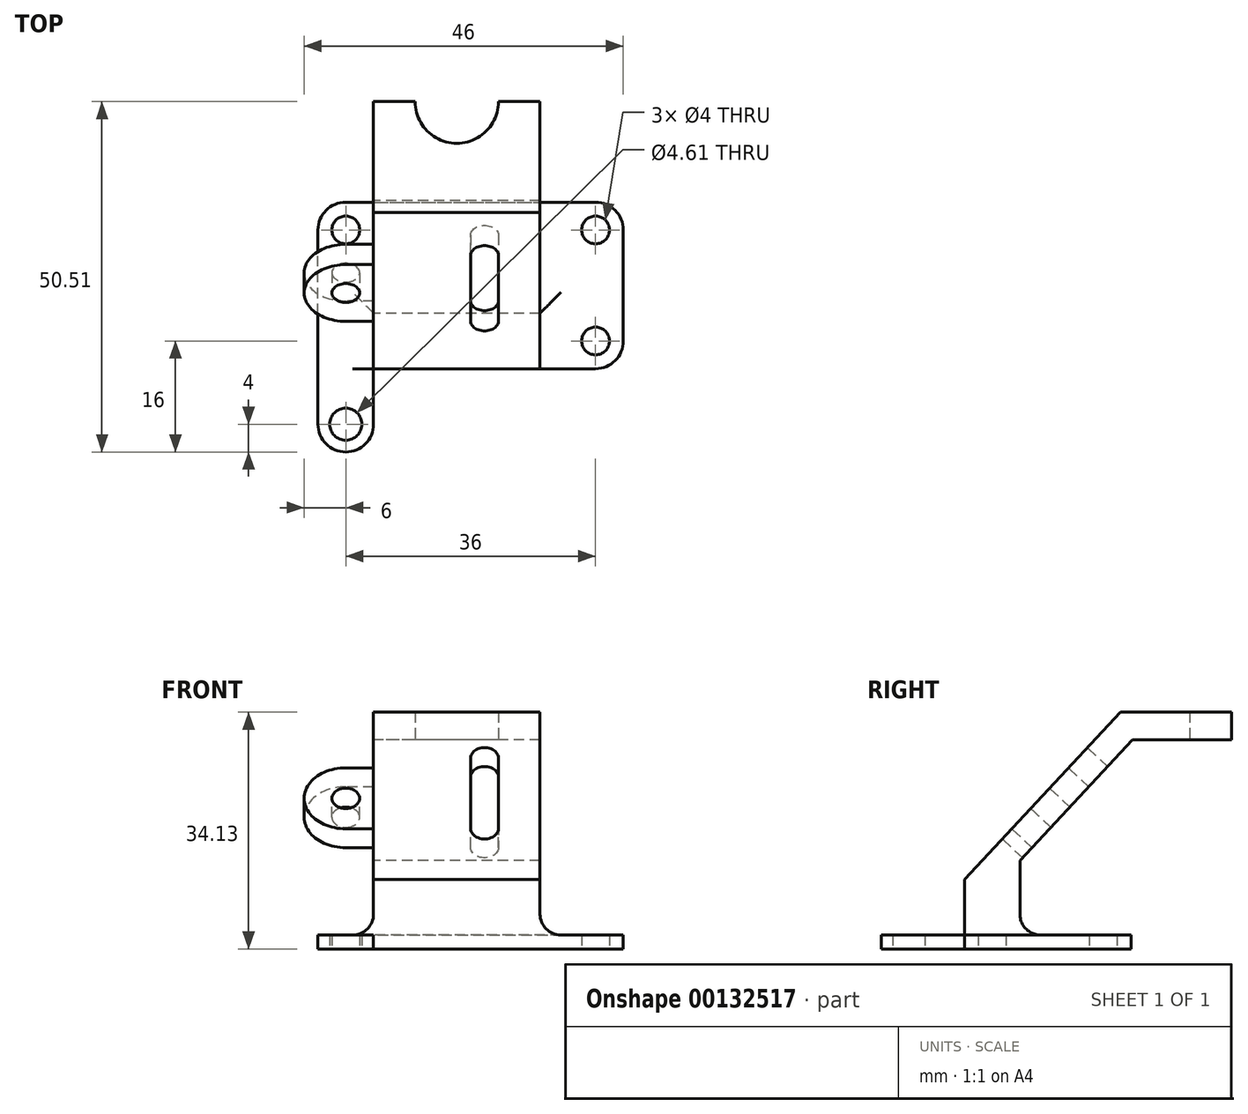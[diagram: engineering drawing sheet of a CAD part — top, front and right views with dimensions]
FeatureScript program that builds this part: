
annotation { "Feature Type Name" : "Feature", "Feature Type Description" : "" }
export const myFeature = defineFeature(function(context is Context, id is Id, definition is map)
    precondition{}
    {
        {
            var Q0;
            Q0=qCreatedBy(makeId("Top.planeOp"),FACE);
            var sketch = newSketch(context, id + "F0", { "sketchPlane" : qUnion([Q0])});
            skLineSegment(sketch, "E0", {"start": v(0, 0) * mm, "end": v(0, 24) * mm});
            skLineSegment(sketch, "E1", {"start": v(0, 24) * mm, "end": v(44, 24) * mm});
            skLineSegment(sketch, "E2", {"start": v(44, 24) * mm, "end": v(44, 0) * mm});
            skLineSegment(sketch, "E3", {"start": v(44, 0) * mm, "end": v(8, 0) * mm});
            skLineSegment(sketch, "E4", {"start": v(8, 0) * mm, "end": v(8, -8) * mm});
            skLineSegment(sketch, "E5", {"start": v(0, 0) * mm, "end": v(0, -8) * mm});
            skArc(sketch, "E6", {"start": v(0, -8) * mm, "mid": v(4, -12) * mm, "end": v(8, -8) * mm});
            skCircle(sketch, "E7", {"center": v(4, -8) * mm, "radius": 2.3 * mm});
            skCircle(sketch, "E8", {"center": v(40, 4) * mm, "radius": 2 * mm});
            skCircle(sketch, "E9", {"center": v(40, 20) * mm, "radius": 2 * mm});
            skCircle(sketch, "E10", {"center": v(4, 20) * mm, "radius": 2 * mm});
            skSolve(sketch);
        }
        {
            var Q0;
            Q0=makeQuery(id+"F0.imprint","IMPRINT",FACE,{"disambiguationData":[TD([[makeQuery(id+"F0.imprint","IMPRINT",EDGE,{"derivedFrom":sQuery(id+"F0.wireOp",EDGE,"E0")}),-1.0]])]});
            extrude(context, id + "F1", {"entities" : qUnion([Q0]), "depth" : 2 * mm});
        }
        {
            var Q0;
            Q0=makeQuery(id+"F1.opExtrude","SWEPT_FACE",FACE,{"disambiguationData":[OSD([sQuery(id+"F0.wireOp",EDGE,"E4")])]});
            var sketch = newSketch(context, id + "F2", { "sketchPlane" : qUnion([Q0])});
            skLineSegment(sketch, "E11", {"start": v(0, 0) * mm, "end": v(0, 10) * mm});
            skLineSegment(sketch, "E12", {"start": v(0, 10) * mm, "end": v(22.5, 34.13) * mm});
            skLineSegment(sketch, "E13", {"start": v(22.5, 34.13) * mm, "end": v(38.5, 34.13) * mm});
            skLineSegment(sketch, "E14", {"start": v(38.5, 34.13) * mm, "end": v(38.5, 30.13) * mm});
            skLineSegment(sketch, "E15", {"start": v(38.5, 30.13) * mm, "end": v(24.25, 30.13) * mm});
            skLineSegment(sketch, "E16", {"start": v(24.25, 30.13) * mm, "end": v(8, 12.71) * mm});
            skLineSegment(sketch, "E17", {"start": v(8, 12.71) * mm, "end": v(8, 0) * mm});
            skLineSegment(sketch, "E18", {"start": v(8, 0) * mm, "end": v(0, 0) * mm});
            skLineSegment(sketch, "E19", {"start": v(8, 12.71) * mm, "end": v(28.06, 12.71) * mm, "construction": true});
            skSolve(sketch);
        }
        {
            var Q0;
            {var subQ0=sQuery(id+"F2.wireOp",EDGE,"E12");Q0=makeQuery(id+"F2.imprint","IMPRINT",FACE,{"disambiguationData":[TD([[makeQuery(id+"F2.imprint","IMPRINT",EDGE,{"derivedFrom":subQ0}),-1.0]])]});}
            extrude(context, id + "F3", {"entities" : qUnion([Q0]), "operationType" : NewBodyOperationType.ADD, "depth" : 24 * mm});
        }
        {
            var Q0;
            Q0=makeQuery(id+"F3.opExtrude","SWEPT_FACE",FACE,{"disambiguationData":[OSD([sQuery(id+"F2.wireOp",EDGE,"E12")])]});
            var sketch = newSketch(context, id + "F4", { "sketchPlane" : qUnion([Q0])});
            skLineSegment(sketch, "E20", {"start": v(8, 7.31) * mm, "end": v(32, 7.31) * mm});
            skLineSegment(sketch, "E21", {"start": v(32, 7.31) * mm, "end": v(32, 40.31) * mm});
            skLineSegment(sketch, "E22", {"start": v(32, 40.31) * mm, "end": v(8, 40.31) * mm});
            skLineSegment(sketch, "E23", {"start": v(8, 40.31) * mm, "end": v(8, 29.31) * mm});
            skLineSegment(sketch, "E24", {"start": v(8, 29.31) * mm, "end": v(4, 29.31) * mm});
            skLineSegment(sketch, "E25", {"start": v(8, 7.31) * mm, "end": v(8, 17.31) * mm});
            skLineSegment(sketch, "E26", {"start": v(8, 17.31) * mm, "end": v(4, 17.31) * mm});
            skArc(sketch, "E27", {"start": v(4, 29.31) * mm, "mid": v(-2, 23.31) * mm, "end": v(4, 17.31) * mm});
            skCircle(sketch, "E28", {"center": v(4, 23.31) * mm, "radius": 2 * mm});
            skLineSegment(sketch, "E29", {"start": v(22, 17.31) * mm, "end": v(22, 31.31) * mm});
            skLineSegment(sketch, "E30", {"start": v(26, 31.31) * mm, "end": v(26, 17.31) * mm});
            skArc(sketch, "E31", {"start": v(26, 31.31) * mm, "mid": v(24, 33.31) * mm, "end": v(22, 31.31) * mm});
            skArc(sketch, "E32", {"start": v(22, 17.31) * mm, "mid": v(24, 15.31) * mm, "end": v(26, 17.31) * mm});
            skSolve(sketch);
        }
        {
            var Q0;
            {var subQ1=sQuery(id+"F4.wireOp",EDGE,"E24");Q0=makeQuery(id+"F4.imprint","IMPRINT",FACE,{"disambiguationData":[TD([[makeQuery(id+"F4.imprint","IMPRINT",EDGE,{"derivedFrom":subQ1}),1.0]])]});}
            extrude(context, id + "F5", {"entities" : qUnion([Q0]), "oppositeDirection" : true, "depth" : 4 * mm});
        }
        {
            var Q0;
            Q0=makeQuery(id+"F4.imprint","IMPRINT",FACE,{"disambiguationData":[TD([[makeQuery(id+"F4.imprint","IMPRINT",EDGE,{"derivedFrom":sQuery(id+"F4.wireOp",EDGE,"E29")}),-1.0]])]});
            extrude(context, id + "F6", {"entities" : qUnion([Q0]), "operationType" : NewBodyOperationType.REMOVE, "endBound" : BoundingType.UP_TO_NEXT, "oppositeDirection" : true, "depth" : 25 * mm});
        }
        {
            var Q0;
            Q0=makeQuery(id+"F3.boolean.opBoolean","INTERSECT",EDGE,{"derivedFrom":[makeQuery(id+"F1.opExtrude","CAP_FACE",FACE,{"disambiguationData":[OSD([sQuery(id+"F0.wireOp",EDGE,"E0"),sQuery(id+"F0.wireOp",EDGE,"E1"),sQuery(id+"F0.wireOp",EDGE,"E2"),sQuery(id+"F0.wireOp",EDGE,"E3"),sQuery(id+"F0.wireOp",EDGE,"E4"),sQuery(id+"F0.wireOp",EDGE,"E5"),sQuery(id+"F0.wireOp",EDGE,"E6"),sQuery(id+"F0.wireOp",EDGE,"E7"),sQuery(id+"F0.wireOp",EDGE,"E8"),sQuery(id+"F0.wireOp",EDGE,"E9"),sQuery(id+"F0.wireOp",EDGE,"E10")])],"isStart":false}),makeQuery(id+"F3.opExtrude","CAP_FACE",FACE,{"disambiguationData":[OSD([sQuery(id+"F2.wireOp",EDGE,"E11"),sQuery(id+"F2.wireOp",EDGE,"E12"),sQuery(id+"F2.wireOp",EDGE,"E13"),sQuery(id+"F2.wireOp",EDGE,"E14"),sQuery(id+"F2.wireOp",EDGE,"E15"),sQuery(id+"F2.wireOp",EDGE,"E16"),sQuery(id+"F2.wireOp",EDGE,"E17"),sQuery(id+"F2.wireOp",EDGE,"E18")])],"isStart":false})]});
            fillet(context, id + "F7", {"entities" : qUnion([Q0]), "radius" : 3 * mm, "tangentPropagation" : true, "allowEdgeOverflow" : false});
        }
        {
            var Q0;
            Q0=makeQuery(id+"F1.opExtrude","SWEPT_EDGE",EDGE,{"disambiguationData":[OSD([sQuery(id+"F0.wireOp",EDGE,"E2"),sQuery(id+"F0.wireOp",EDGE,"E3")])]});
            fillet(context, id + "F8", {"entities" : qUnion([Q0]), "radius" : 4 * mm, "tangentPropagation" : true, "allowEdgeOverflow" : false});
        }
        {
            var Q0;
            Q0=makeQuery(id+"F1.opExtrude","SWEPT_EDGE",EDGE,{"disambiguationData":[OSD([sQuery(id+"F0.wireOp",EDGE,"E1"),sQuery(id+"F0.wireOp",EDGE,"E2")])]});
            fillet(context, id + "F9", {"entities" : qUnion([Q0]), "radius" : 4 * mm, "tangentPropagation" : true, "allowEdgeOverflow" : false});
        }
        {
            var Q0;
            Q0=makeQuery(id+"F1.opExtrude","SWEPT_EDGE",EDGE,{"disambiguationData":[OSD([sQuery(id+"F0.wireOp",EDGE,"E0"),sQuery(id+"F0.wireOp",EDGE,"E1")])]});
            fillet(context, id + "F10", {"entities" : qUnion([Q0]), "radius" : 4 * mm, "tangentPropagation" : true, "allowEdgeOverflow" : false});
        }
        {
            var Q0;
            Q0=makeQuery(id+"F3.boolean.opBoolean","INTERSECT",EDGE,{"derivedFrom":[makeQuery(id+"F1.opExtrude","CAP_FACE",FACE,{"disambiguationData":[OSD([sQuery(id+"F0.wireOp",EDGE,"E0"),sQuery(id+"F0.wireOp",EDGE,"E1"),sQuery(id+"F0.wireOp",EDGE,"E2"),sQuery(id+"F0.wireOp",EDGE,"E3"),sQuery(id+"F0.wireOp",EDGE,"E4"),sQuery(id+"F0.wireOp",EDGE,"E5"),sQuery(id+"F0.wireOp",EDGE,"E6"),sQuery(id+"F0.wireOp",EDGE,"E7"),sQuery(id+"F0.wireOp",EDGE,"E8"),sQuery(id+"F0.wireOp",EDGE,"E9"),sQuery(id+"F0.wireOp",EDGE,"E10")])],"isStart":false}),makeQuery(id+"F3.opExtrude","SWEPT_FACE",FACE,{"disambiguationData":[OSD([sQuery(id+"F2.wireOp",EDGE,"E17")])]})]});
            fillet(context, id + "F11", {"entities" : qUnion([Q0]), "radius" : 3 * mm, "tangentPropagation" : true, "allowEdgeOverflow" : false});
        }
        {
            var Q0;
            Q0=makeQuery(id+"F3.boolean.opBoolean","INTERSECT",EDGE,{"derivedFrom":[makeQuery(id+"F1.opExtrude","CAP_FACE",FACE,{"disambiguationData":[OSD([sQuery(id+"F0.wireOp",EDGE,"E0"),sQuery(id+"F0.wireOp",EDGE,"E1"),sQuery(id+"F0.wireOp",EDGE,"E2"),sQuery(id+"F0.wireOp",EDGE,"E3"),sQuery(id+"F0.wireOp",EDGE,"E4"),sQuery(id+"F0.wireOp",EDGE,"E5"),sQuery(id+"F0.wireOp",EDGE,"E6"),sQuery(id+"F0.wireOp",EDGE,"E7"),sQuery(id+"F0.wireOp",EDGE,"E8"),sQuery(id+"F0.wireOp",EDGE,"E9"),sQuery(id+"F0.wireOp",EDGE,"E10")])],"isStart":false}),makeQuery(id+"F3.opExtrude","CAP_FACE",FACE,{"disambiguationData":[OSD([sQuery(id+"F2.wireOp",EDGE,"E11"),sQuery(id+"F2.wireOp",EDGE,"E12"),sQuery(id+"F2.wireOp",EDGE,"E13"),sQuery(id+"F2.wireOp",EDGE,"E14"),sQuery(id+"F2.wireOp",EDGE,"E15"),sQuery(id+"F2.wireOp",EDGE,"E16"),sQuery(id+"F2.wireOp",EDGE,"E17"),sQuery(id+"F2.wireOp",EDGE,"E18")])],"isStart":true})]});
            fillet(context, id + "F12", {"entities" : qUnion([Q0]), "radius" : 3 * mm, "tangentPropagation" : true, "allowEdgeOverflow" : false});
        }
        {
            var Q0;
            Q0=qCreatedBy(makeId("Top.planeOp"),FACE);
            var sketch = newSketch(context, id + "F13", { "sketchPlane" : qUnion([Q0])});
            skLineSegment(sketch, "E33", {"start": v(0, 0) * mm, "end": v(44, 0) * mm});
            skLineSegment(sketch, "E34", {"start": v(44, 0) * mm, "end": v(44, 38.5) * mm});
            skLineSegment(sketch, "E35", {"start": v(44, 38.5) * mm, "end": v(0, 38.5) * mm});
            skLineSegment(sketch, "E36", {"start": v(0, 38.5) * mm, "end": v(0, 0) * mm});
            skArc(sketch, "E37", {"start": v(14, 38.5) * mm, "mid": v(20, 32.5) * mm, "end": v(26, 38.5) * mm});
            skLineSegment(sketch, "E38", {"start": v(14, 38.5) * mm, "end": v(26, 38.5) * mm});
            skSolve(sketch);
        }
        {
            var Q0;
            Q0=makeQuery(id+"F13.imprint","IMPRINT",FACE,{"disambiguationData":[TD([[makeQuery(id+"F13.imprint","IMPRINT",EDGE,{"derivedFrom":sQuery(id+"F13.wireOp",EDGE,"E37")}),1.0]])]});
            var Q1;
            Q1=sQuery(id+"F13.wireOp",EDGE,"E37");
            var Q2;
            Q2=sQuery(id+"F13.wireOp",EDGE,"E38");
            extrude(context, id + "F14", {"entities" : qUnion([Q0]), "operationType" : NewBodyOperationType.REMOVE, "surfaceEntities" : qUnion([Q1, Q2]), "endBound" : BoundingType.THROUGH_ALL, "depth" : 25 * mm});
        }
    });
